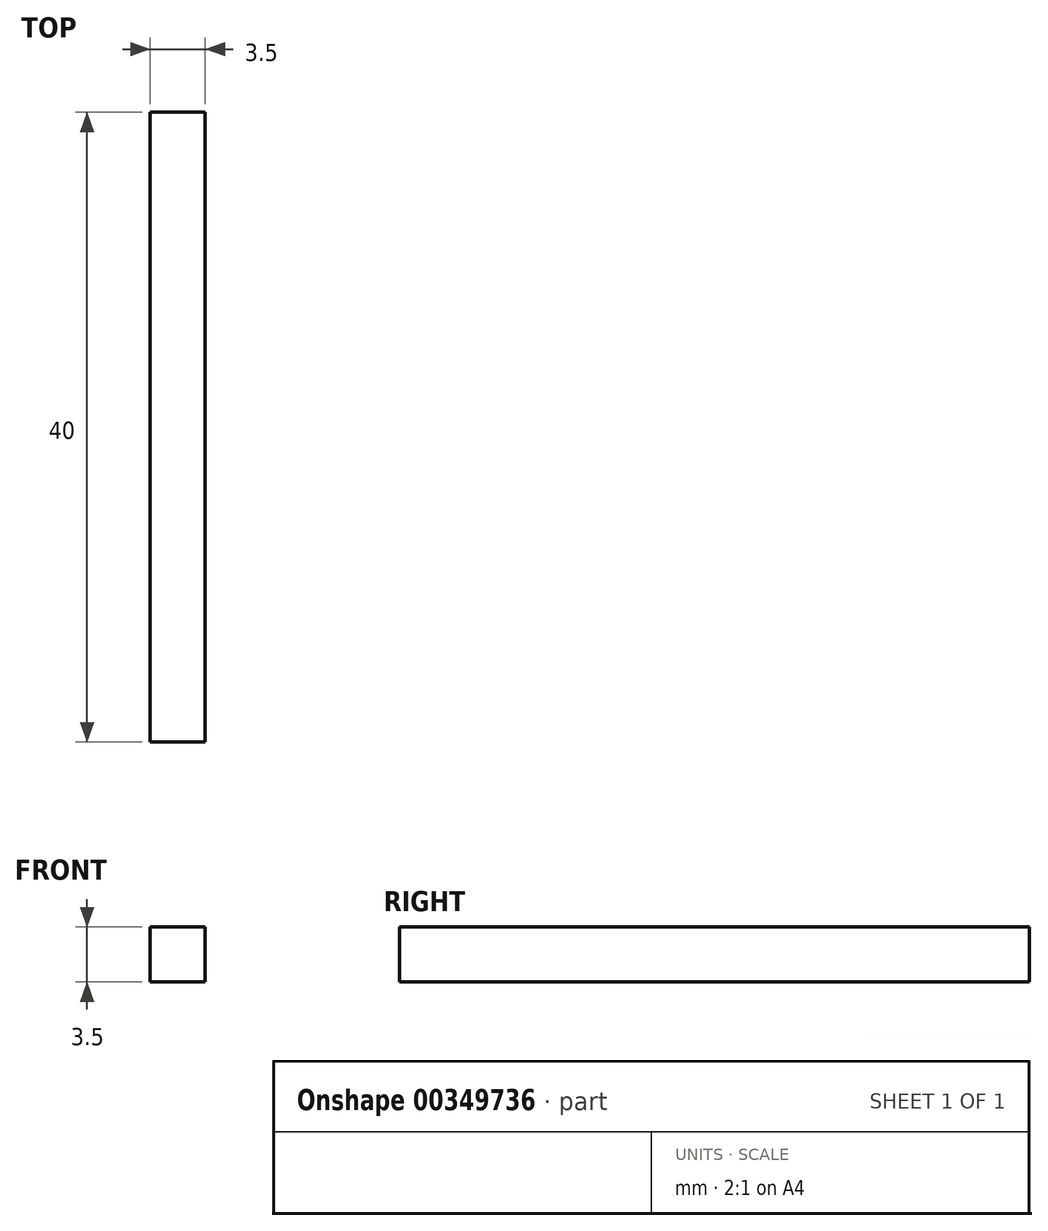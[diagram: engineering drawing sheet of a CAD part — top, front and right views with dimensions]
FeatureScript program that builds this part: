
annotation { "Feature Type Name" : "Feature", "Feature Type Description" : "" }
export const myFeature = defineFeature(function(context is Context, id is Id, definition is map)
    precondition{}
    {
        {
            var Q0;
            Q0=qCreatedBy(makeId("Top.planeOp"),FACE);
            var sketch = newSketch(context, id + "F0", { "sketchPlane" : qUnion([Q0])});
            skLineSegment(sketch, "E0.bottom", {"start": v(1.75, -20) * mm, "end": v(-1.75, -20) * mm});
            skLineSegment(sketch, "E0.top", {"start": v(1.75, 20) * mm, "end": v(-1.75, 20) * mm});
            skLineSegment(sketch, "E0.left", {"start": v(1.75, -20) * mm, "end": v(1.75, 20) * mm});
            skLineSegment(sketch, "E0.right", {"start": v(-1.75, -20) * mm, "end": v(-1.75, 20) * mm});
            skPoint(sketch, "E0.middle", {"position": v(0, 0) * mm});
            skSolve(sketch);
        }
        {
            var Q0;
            Q0=qSketchRegion(id+"F0",true);
            extrude(context, id + "F1", {"entities" : qUnion([Q0]), "depth" : 3.5 * mm});
        }
    });
